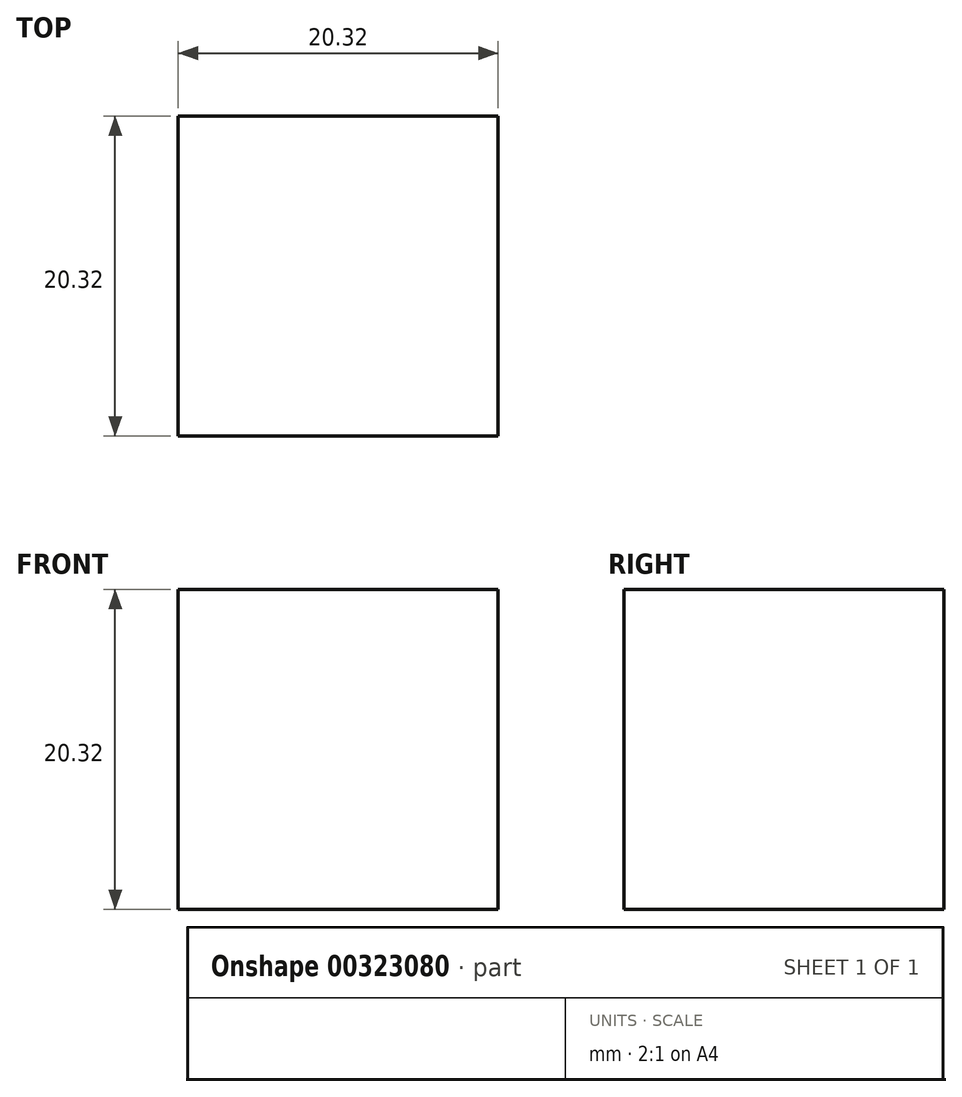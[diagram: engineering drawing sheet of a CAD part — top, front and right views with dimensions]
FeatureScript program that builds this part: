
annotation { "Feature Type Name" : "Feature", "Feature Type Description" : "" }
export const myFeature = defineFeature(function(context is Context, id is Id, definition is map)
    precondition{}
    {
        {
            var Q0;
            Q0=qCreatedBy(makeId("Top.planeOp"),FACE);
            var sketch = newSketch(context, id + "F0", { "sketchPlane" : qUnion([Q0])});
            skLineSegment(sketch, "E0.bottom", {"start": v(-10.16, 10.16) * mm, "end": v(10.16, 10.16) * mm});
            skLineSegment(sketch, "E0.top", {"start": v(-10.16, -10.16) * mm, "end": v(10.16, -10.16) * mm});
            skLineSegment(sketch, "E0.left", {"start": v(-10.16, 10.16) * mm, "end": v(-10.16, -10.16) * mm});
            skLineSegment(sketch, "E0.right", {"start": v(10.16, 10.16) * mm, "end": v(10.16, -10.16) * mm});
            skPoint(sketch, "E0.middle", {"position": v(0, 0) * mm});
            skSolve(sketch);
        }
        {
            var Q0;
            Q0=makeQuery(id+"F0.imprint","IMPRINT",FACE,{"disambiguationData":[TD([[makeQuery(id+"F0.imprint","IMPRINT",EDGE,{"derivedFrom":sQuery(id+"F0.wireOp",EDGE,"E0.bottom")}),-1.0]])]});
            extrude(context, id + "F1", {"entities" : qUnion([Q0]), "depth" : 20.32 * mm});
        }
    });
